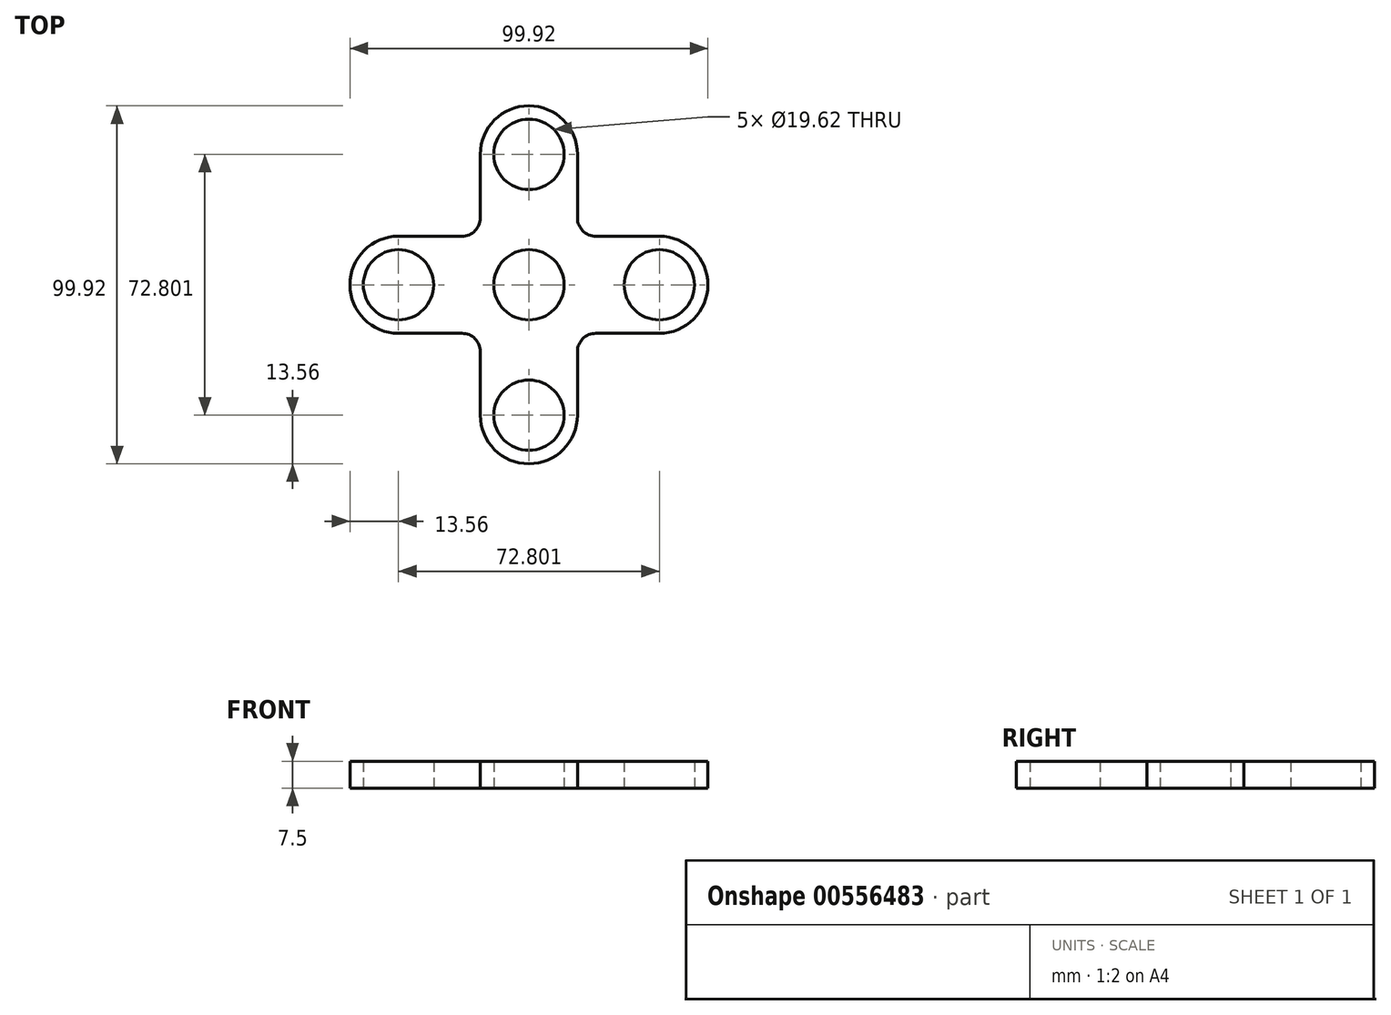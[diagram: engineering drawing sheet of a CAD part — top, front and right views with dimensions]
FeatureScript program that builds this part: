
annotation { "Feature Type Name" : "Feature", "Feature Type Description" : "" }
export const myFeature = defineFeature(function(context is Context, id is Id, definition is map)
    precondition{}
    {
        {
            var Q0;
            Q0=qCreatedBy(makeId("Top.planeOp"),FACE);
            var sketch = newSketch(context, id + "F0", { "sketchPlane" : qUnion([Q0])});
            skCircle(sketch, "E0", {"center": v(0, 0) * mm, "radius": 9.81 * mm});
            skCircle(sketch, "E1", {"center": v(0, 36.4) * mm, "radius": 9.81 * mm});
            skCircle(sketch, "E2", {"center": v(36.4, 0) * mm, "radius": 9.81 * mm});
            skCircle(sketch, "E3", {"center": v(0, -36.4) * mm, "radius": 9.81 * mm});
            skCircle(sketch, "E4", {"center": v(-36.4, 0) * mm, "radius": 9.81 * mm});
            skCircle(sketch, "E5", {"center": v(0, 36.4) * mm, "radius": 13.56 * mm});
            skCircle(sketch, "E6", {"center": v(36.4, 0) * mm, "radius": 13.56 * mm});
            skCircle(sketch, "E7", {"center": v(0, -36.4) * mm, "radius": 13.56 * mm});
            skCircle(sketch, "E8", {"center": v(-36.4, 0) * mm, "radius": 13.56 * mm});
            skPoint(sketch, "E9", {"position": v(9.81, 0) * mm});
            skPoint(sketch, "E10", {"position": v(-9.81, 0) * mm});
            skPoint(sketch, "E11", {"position": v(0, 9.81) * mm});
            skPoint(sketch, "E12", {"position": v(0, -9.81) * mm});
            skPoint(sketch, "E13", {"position": v(-13.56, -13.56) * mm});
            skPoint(sketch, "E14", {"position": v(-13.56, 13.56) * mm});
            skPoint(sketch, "E15", {"position": v(13.56, 13.56) * mm});
            skPoint(sketch, "E16", {"position": v(13.56, -13.56) * mm});
            skPoint(sketch, "E17", {"position": v(-13.56, -36.4) * mm});
            skPoint(sketch, "E18", {"position": v(-13.56, 36.4) * mm});
            skPoint(sketch, "E19", {"position": v(13.56, 36.4) * mm});
            skPoint(sketch, "E20", {"position": v(13.56, -36.4) * mm});
            skPoint(sketch, "E21", {"position": v(36.4, -13.56) * mm});
            skPoint(sketch, "E22", {"position": v(36.4, 13.56) * mm});
            skPoint(sketch, "E23", {"position": v(-36.4, 13.56) * mm});
            skPoint(sketch, "E24", {"position": v(-36.4, -13.56) * mm});
            skLineSegment(sketch, "E25", {"start": v(-13.56, -36.4) * mm, "end": v(-13.56, -13.56) * mm});
            skLineSegment(sketch, "E26", {"start": v(13.56, -36.4) * mm, "end": v(13.56, -13.56) * mm});
            skLineSegment(sketch, "E27", {"start": v(36.4, -13.56) * mm, "end": v(13.56, -13.56) * mm});
            skLineSegment(sketch, "E28", {"start": v(13.56, 13.56) * mm, "end": v(36.4, 13.56) * mm});
            skLineSegment(sketch, "E29", {"start": v(13.56, 13.56) * mm, "end": v(13.56, 36.4) * mm});
            skLineSegment(sketch, "E30", {"start": v(-13.56, 36.4) * mm, "end": v(-13.56, 13.56) * mm});
            skLineSegment(sketch, "E31", {"start": v(-13.56, 13.56) * mm, "end": v(-36.4, 13.56) * mm});
            skLineSegment(sketch, "E32", {"start": v(-36.4, -13.56) * mm, "end": v(-13.56, -13.56) * mm});
            skSolve(sketch);
        }
        {
            var Q0;
            Q0 = qSketchRegion(id + "F0", true);
            extrude(context, id + "F1", {"entities" : qUnion([Q0]), "depth" : 7.5 * mm, "offsetDistance" : 25.4 * mm});
        }
        {
            var Q0;
            Q0=makeQuery(id+"F1.opExtrude","SWEPT_EDGE",EDGE,{"disambiguationData":[OSD([sQuery(id+"F0.wireOp",EDGE,"E30"),sQuery(id+"F0.wireOp",EDGE,"E31")])]});
            fillet(context, id + "F2", {"entities" : qUnion([Q0]), "radius" : 5.08 * mm, "tangentPropagation" : true, "allowEdgeOverflow" : false});
        }
        {
            var Q0;
            Q0=makeQuery(id+"F1.opExtrude","SWEPT_EDGE",EDGE,{"disambiguationData":[OSD([sQuery(id+"F0.wireOp",EDGE,"E28"),sQuery(id+"F0.wireOp",EDGE,"E29")])]});
            fillet(context, id + "F3", {"entities" : qUnion([Q0]), "radius" : 5.08 * mm, "tangentPropagation" : true, "allowEdgeOverflow" : false});
        }
        {
            var Q0;
            Q0=makeQuery(id+"F1.opExtrude","SWEPT_EDGE",EDGE,{"disambiguationData":[OSD([sQuery(id+"F0.wireOp",EDGE,"E25"),sQuery(id+"F0.wireOp",EDGE,"E32")])]});
            fillet(context, id + "F4", {"entities" : qUnion([Q0]), "radius" : 5.08 * mm, "tangentPropagation" : true, "allowEdgeOverflow" : false});
        }
        {
            var Q0;
            Q0=makeQuery(id+"F1.opExtrude","SWEPT_EDGE",EDGE,{"disambiguationData":[OSD([sQuery(id+"F0.wireOp",EDGE,"E26"),sQuery(id+"F0.wireOp",EDGE,"E27")])]});
            fillet(context, id + "F5", {"entities" : qUnion([Q0]), "radius" : 5.08 * mm, "tangentPropagation" : true, "allowEdgeOverflow" : false});
        }
    });
